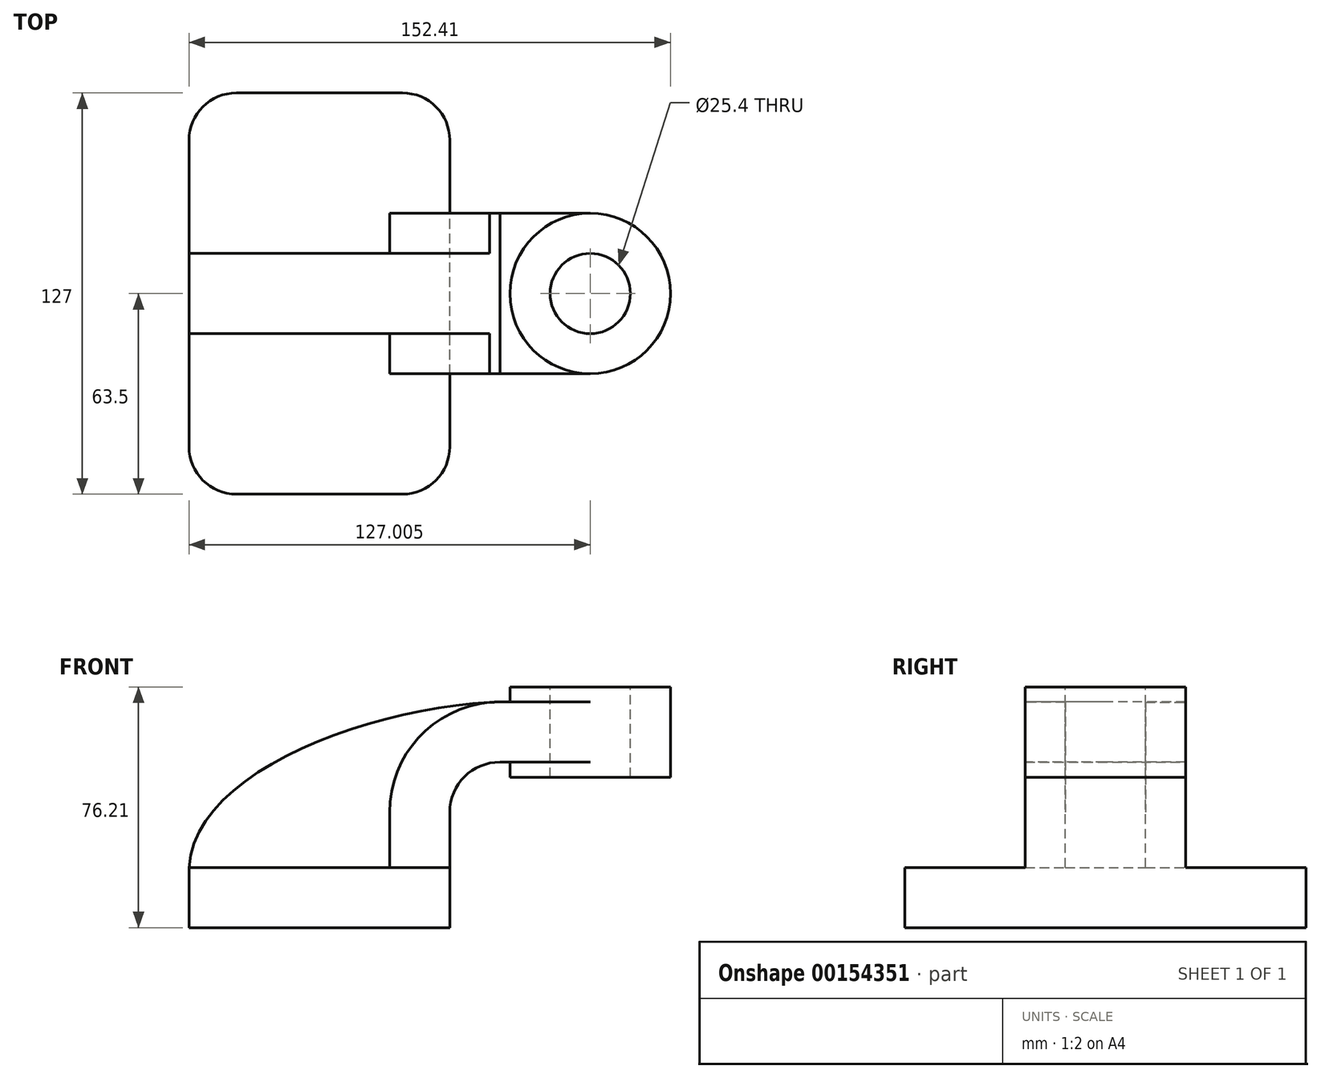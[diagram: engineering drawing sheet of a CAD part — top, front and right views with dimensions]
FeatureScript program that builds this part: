
annotation { "Feature Type Name" : "Feature", "Feature Type Description" : "" }
export const myFeature = defineFeature(function(context is Context, id is Id, definition is map)
    precondition{}
    {
        {
            var Q0;
            Q0=qCreatedBy(makeId("Front.planeOp"),FACE);
            var sketch = newSketch(context, id + "F0", { "sketchPlane" : qUnion([Q0])});
            skLineSegment(sketch, "E0.rect.bottom", {"start": v(-41.28, 9.52) * mm, "end": v(41.28, 9.52) * mm});
            skLineSegment(sketch, "E0.rect.top", {"start": v(-41.28, -9.52) * mm, "end": v(41.28, -9.52) * mm});
            skLineSegment(sketch, "E0.rect.left", {"start": v(-41.28, 9.52) * mm, "end": v(-41.28, -9.52) * mm});
            skLineSegment(sketch, "E0.rect.right", {"start": v(41.28, 9.52) * mm, "end": v(41.28, -9.52) * mm});
            skPoint(sketch, "E0.rect.middle", {"position": v(0, 0) * mm});
            skLineSegment(sketch, "E1", {"start": v(41.28, 9.52) * mm, "end": v(41.28, 27) * mm});
            skArc(sketch, "E2", {"start": v(41.28, 27) * mm, "mid": v(45.92, 38.23) * mm, "end": v(57.15, 42.88) * mm});
            skLineSegment(sketch, "E3", {"start": v(57.15, 42.88) * mm, "end": v(85.72, 42.88) * mm});
            skLineSegment(sketch, "E4.rect.bottom", {"start": v(60.32, 38.1) * mm, "end": v(111.12, 38.1) * mm});
            skLineSegment(sketch, "E4.rect.top", {"start": v(60.32, 66.68) * mm, "end": v(111.12, 66.68) * mm});
            skLineSegment(sketch, "E4.rect.left", {"start": v(60.32, 38.1) * mm, "end": v(60.32, 66.68) * mm});
            skLineSegment(sketch, "E4.rect.right", {"start": v(111.13, 38.1) * mm, "end": v(111.12, 66.68) * mm});
            skPoint(sketch, "E4.rect.middle", {"position": v(85.72, 52.39) * mm});
            skLineSegment(sketch, "E5.0", {"start": v(57.15, 61.93) * mm, "end": v(85.72, 61.93) * mm});
            skArc(sketch, "E5.1", {"start": v(22.23, 27) * mm, "mid": v(32.45, 51.7) * mm, "end": v(57.15, 61.93) * mm});
            skLineSegment(sketch, "E5.2", {"start": v(22.23, 9.52) * mm, "end": v(22.23, 27) * mm});
            skLineSegment(sketch, "E6", {"start": v(85.72, 38.1) * mm, "end": v(85.72, 66.68) * mm});
            skFitSpline(sketch, "E7", {"points": [v(-41.28, 9.53) * mm, v(57.15, 61.93) * mm], "startDerivative": vector(5.2, 92.34) * mm, "endDerivative": vector(120.92, 4.22) * mm});
            skSolve(sketch);
        }
        {
            var Q0;
            Q0=makeQuery(id+"F0.imprint","IMPRINT",FACE,{"disambiguationData":[TD([[makeQuery(id+"F0.imprint","IMPRINT",EDGE,{"derivedFrom":sQuery(id+"F0.wireOp",EDGE,"E0.rect.top")}),1.0]])]});
            extrude(context, id + "F1", {"entities" : qUnion([Q0]), "endBound" : BoundingType.SYMMETRIC, "depth" : 127 * mm});
        }
        {
            var Q0;
            {var subQ9=sQuery(id+"F0.wireOp",EDGE,"E1");Q0=makeQuery(id+"F0.imprint","IMPRINT",FACE,{"disambiguationData":[TD([[makeQuery(id+"F0.imprint","IMPRINT",EDGE,{"derivedFrom":subQ9}),1.0]])]});}
            var Q1;
            {var subQ0=sQuery(id+"F0.wireOp",EDGE,"E6");var subQ1=sQuery(id+"F0.wireOp",EDGE,"E3");var subQ2=makeQuery(id+"F0.imprint","INTERSECT",VERTEX,{"derivedFrom":[subQ1,subQ0]});Q1=makeQuery(id+"F0.imprint","IMPRINT",FACE,{"disambiguationData":[TD([[makeQuery(id+"F0.imprint","IMPRINT",EDGE,{"disambiguationData":[TD([[subQ2,1.0]])],"derivedFrom":subQ1}),1.0]])]});}
            extrude(context, id + "F2", {"entities" : qUnion([Q0, Q1]), "operationType" : NewBodyOperationType.ADD, "endBound" : BoundingType.SYMMETRIC, "depth" : 50.8 * mm});
        }
        {
            var Q0;
            {var subQ3=sQuery(id+"F0.wireOp",EDGE,"E5.2");Q0=makeQuery(id+"F0.imprint","IMPRINT",FACE,{"disambiguationData":[TD([[makeQuery(id+"F0.imprint","IMPRINT",EDGE,{"derivedFrom":subQ3}),1.0]])]});}
            extrude(context, id + "F3", {"entities" : qUnion([Q0]), "operationType" : NewBodyOperationType.ADD, "endBound" : BoundingType.SYMMETRIC, "depth" : 25.4 * mm});
        }
        {
            var Q0;
            {var subQ5=sQuery(id+"F0.wireOp",EDGE,"E4.rect.right");Q0=makeQuery(id+"F0.imprint","IMPRINT",FACE,{"disambiguationData":[TD([[makeQuery(id+"F0.imprint","IMPRINT",EDGE,{"derivedFrom":subQ5}),1.0]])]});}
            var Q1;
            Q1=sQuery(id+"F0.wireOp",EDGE,"E6");
            revolve(context, id + "F4", {"operationType" : NewBodyOperationType.ADD, "entities" : qUnion([Q0]), "axis" : qUnion([Q1]), "revolveType" : RevolveType.FULL});
        }
        {
            var Q0;
            Q0=makeQuery(id+"F1.opExtrude","CAP_EDGE",EDGE,{"disambiguationData":[OSD([sQuery(id+"F0.wireOp",EDGE,"E0.rect.right")])],"isStart":false});
            var Q1;
            Q1=makeQuery(id+"F1.opExtrude","CAP_EDGE",EDGE,{"disambiguationData":[OSD([sQuery(id+"F0.wireOp",EDGE,"E0.rect.left")])],"isStart":false});
            var Q2;
            Q2=makeQuery(id+"F1.opExtrude","CAP_EDGE",EDGE,{"disambiguationData":[OSD([sQuery(id+"F0.wireOp",EDGE,"E0.rect.right")])],"isStart":true});
            var Q3;
            Q3=makeQuery(id+"F1.opExtrude","CAP_EDGE",EDGE,{"disambiguationData":[OSD([sQuery(id+"F0.wireOp",EDGE,"E0.rect.left")])],"isStart":true});
            fillet(context, id + "F5", {"entities" : qUnion([Q0, Q1, Q2, Q3]), "radius" : 15 * mm, "tangentPropagation" : true, "allowEdgeOverflow" : false});
        }
        {
            var Q0;
            Q0=makeQuery(id+"F4.opRevolve","SWEPT_FACE",FACE,{"disambiguationData":[OSD([sQuery(id+"F0.wireOp",EDGE,"E4.rect.top")])]});
            var sketch = newSketch(context, id + "F6", { "sketchPlane" : qUnion([Q0])});
            skPoint(sketch, "E8", {"position": v(85.72, 0) * mm});
            skSolve(sketch);
        }
        {
            var Q0;
            Q0=sQuery(id+"F6.wireOp",VERTEX,"E8");
            var Q1;
            Q1=makeQuery(id+"F1.opExtrude","SWEPT_BODY",BODY,{"disambiguationData":[OSD([sQuery(id+"F0.wireOp",EDGE,"E0.rect.bottom"),sQuery(id+"F0.wireOp",EDGE,"E0.rect.top"),sQuery(id+"F0.wireOp",EDGE,"E0.rect.left"),sQuery(id+"F0.wireOp",EDGE,"E0.rect.right")])]});
            hole(context, id + "F7", {"style" : HoleStyle.SIMPLE, "endStyle" : HoleEndStyle.THROUGH, "holeDiameter" : 25.4 * mm, "locations" : qUnion([Q0]), "scope" : qUnion([Q1]), "isTappedThrough" : true});
        }
    });
